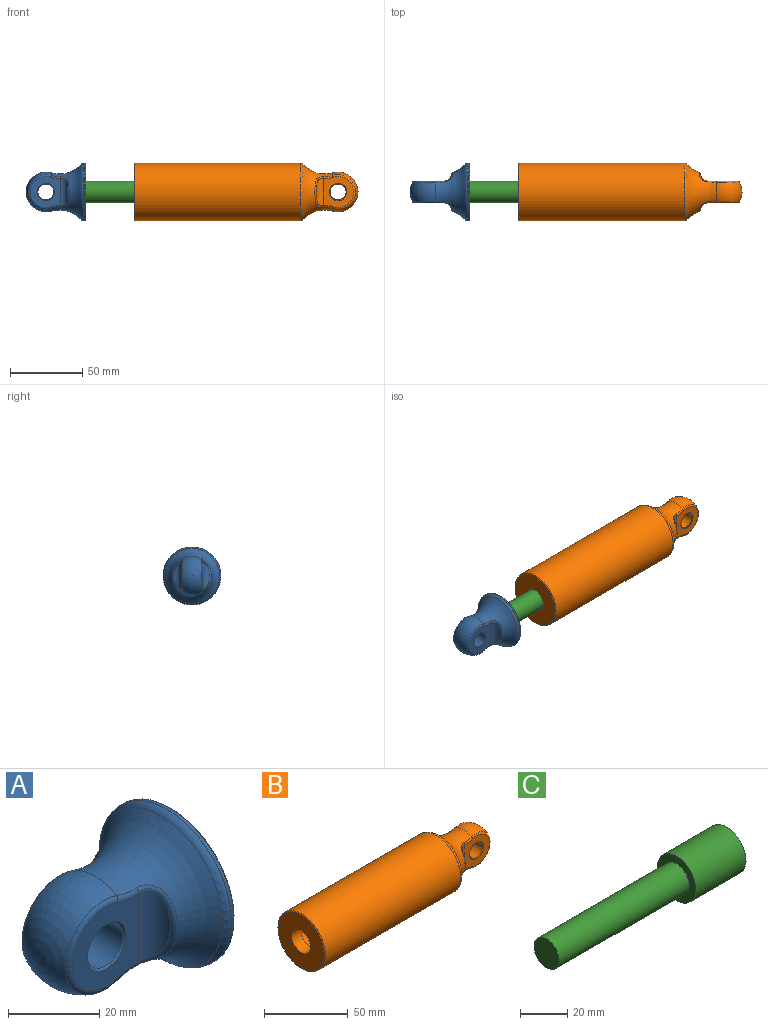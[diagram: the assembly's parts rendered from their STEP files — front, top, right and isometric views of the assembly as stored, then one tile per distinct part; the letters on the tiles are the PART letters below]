
ASSEMBLY  parts=3 mates=2
PART A: 21 faces, bbox 43.1x70.2x70.2 mm
  f0: torus R=32.43mm, axis (-1,0,0), area 1424.8mm2, adj f1,f9,f10,f12,f13,f14,f16,f17
  f1: sphere r=13.75mm, area 690.5mm2, adj f0,f11,f15
  f2: plane 39x39mm, normal (1,0,0), area 1194.6mm2, adj f18
  f3: cylinder r=20mm len=40mm, axis (-1,0,0), area 105mm2, adj f17,f18
  f4: plane 21.36x20.69mm, normal (0,-1,0), area 262mm2, adj f7,f14,f15,f16,f20
  f5: plane 21.36x20.69mm, normal (0,1,0), area 262mm2, adj f8,f10,f11,f12,f19
  f6: cylinder r=5.5mm len=14mm, axis (0,-1,0), area 483.8mm2, adj f19,f20
  f7: cylinder r=5mm len=18.34mm, axis (0,0,-1), area 116.5mm2, adj f4,f13
  f8: cylinder r=5mm len=18.34mm, axis (0,0,1), area 116.5mm2, adj f5,f9
  f9: bspline ~20.84x7.31mm, area 45.1mm2, adj f0,f8,f10,f12
  f10: bspline ~10.74x2.44mm, area 9.8mm2, adj f0,f5,f9,f11
  f11: torus R=10.68mm, axis (0,1,0), area 68.6mm2, adj f1,f5,f10,f12
  f12: bspline ~12.41x3.13mm, area 9.8mm2, adj f0,f5,f9,f11
  f13: bspline ~20.84x7.31mm, area 45.1mm2, adj f0,f7,f14,f16
  f14: bspline ~12.41x3.13mm, area 9.8mm2, adj f0,f4,f13,f15
  f15: torus R=10.68mm, axis (0,1,0), area 68.6mm2, adj f1,f4,f14,f16
  f16: bspline ~10.74x2.44mm, area 9.8mm2, adj f0,f4,f13,f15
  f17: torus R=17.5mm, axis (1,0,0), area 261.7mm2, adj f0,f3
  f18: cone r=20mm half-angle=45deg, axis (-1,0,0), area 87.7mm2, adj f2,f3
  f19: cone r=5.5mm half-angle=45deg, axis (0,1,0), area 25.5mm2, adj f5,f6
  f20: cone r=5.5mm half-angle=45deg, axis (0,-1,0), area 25.5mm2, adj f4,f6
PART B: 25 faces, bbox 154.8x70.2x70.2 mm
  f0: sphere r=13.75mm, area 690.5mm2, adj f1,f15,f19
  f1: torus R=32.43mm, axis (-1,0,0), area 1424.8mm2, adj f0,f13,f14,f16,f17,f18,f20,f21
  f2: cylinder r=20mm len=114.34mm, axis (-1,0,0), area 14367.9mm2, adj f21,f22
  f3: plane 39x39mm, normal (-1,0,0), area 993.5mm2, adj f4,f22
  f4: cylinder r=8mm len=16mm, axis (-1,0,0), area 402.1mm2, adj f3,f5
  f5: plane 24x24mm, normal (1,0,0), area 251.3mm2, adj f4,f6
  f6: cylinder r=12mm len=100mm, axis (-1,0,0), area 7539.8mm2, adj f5,f7
  f7: plane 24x24mm, normal (-1,0,0), area 452.4mm2, adj f6
  f8: plane 21.36x20.69mm, normal (0,-1,0), area 262mm2, adj f11,f18,f19,f20,f24
  f9: plane 21.36x20.69mm, normal (0,1,0), area 262mm2, adj f12,f14,f15,f16,f23
  f10: cylinder r=5.5mm len=14mm, axis (0,-1,0), area 483.8mm2, adj f23,f24
  f11: cylinder r=5mm len=18.34mm, axis (0,0,1), area 116.5mm2, adj f8,f17
  f12: cylinder r=5mm len=18.34mm, axis (0,0,1), area 116.5mm2, adj f9,f13
  f13: bspline ~20.84x7.31mm, area 45.1mm2, adj f1,f12,f14,f16
  f14: bspline ~10.74x2.45mm, area 9.8mm2, adj f1,f9,f13,f15
  f15: torus R=10.68mm, axis (0,-1,0), area 68.6mm2, adj f0,f9,f14,f16
  f16: bspline ~10.74x2.44mm, area 9.8mm2, adj f1,f9,f13,f15
  f17: bspline ~20.84x7.31mm, area 45.1mm2, adj f1,f11,f18,f20
  f18: bspline ~10.74x2.44mm, area 9.8mm2, adj f1,f8,f17,f19
  f19: torus R=10.68mm, axis (0,-1,0), area 68.6mm2, adj f0,f8,f18,f20
  f20: bspline ~10.74x2.45mm, area 9.8mm2, adj f1,f8,f17,f19
  f21: torus R=17.5mm, axis (1,0,0), area 261.7mm2, adj f1,f2
  f22: cone r=19.5mm half-angle=45deg, axis (1,0,0), area 87.7mm2, adj f2,f3
  f23: cone r=6mm half-angle=45deg, axis (0,1,0), area 25.5mm2, adj f9,f10
  f24: cone r=5.5mm half-angle=45deg, axis (0,-1,0), area 25.5mm2, adj f8,f10
PART C: 5 faces, bbox 107.6x23x23 mm
  f0: plane 23x23mm, normal (-1,0,0), area 238.8mm2, adj f1,f4
  f1: cylinder r=7.5mm len=77.6mm, axis (-1,0,0), area 3656.8mm2, adj f0,f2
  f2: plane 15x15mm, normal (-1,0,0), area 176.7mm2, adj f1
  f3: plane 23x23mm, normal (1,0,0), area 415.5mm2, adj f4
  f4: cylinder r=11.5mm len=30mm, axis (-1,0,0), area 2167.7mm2, adj f0,f3
PLACE A t=(142.16,0,0)mm
PLACE B t=(175.59,0,0)mm fixed
PLACE C t=(142.16,0,0)mm
MATE slider C.f1 <-> B.f1  axis (-1,0,0) through (133.66,0,0)mm
MATE fastened A.f0 <-> C.f1  axis (1,0,0) through (26.06,0,0)mm
